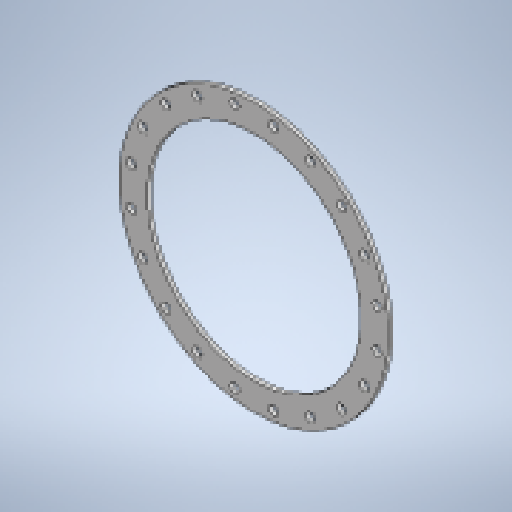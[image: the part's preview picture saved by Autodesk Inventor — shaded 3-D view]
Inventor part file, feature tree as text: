
AUTODESK INVENTOR PART (.ipt)
format: ipt  version: 2025.3 (Build 293356030, 356C)  size: 240,640 bytes
history: native  units: mm
features: sketch x2, other x2, extrude x1, pattern_circular x1, projected_geometry x1
ambient origin geometry x8: Origin, YZ Plane, XZ Plane, XY Plane, X Axis, Y Axis, Z Axis, Center Point
bodies: Solid1 (feature_tree)
feature tree (7):
  extrude  "Extrusion1"  Depth=10.0mm TaperAngle=0.0deg
  pattern_circular  "Circular Pattern1"  Count=31  [1 undecoded]
  sketch  "Sketch1"  dims[d0=512.0mm d1=670.0mm d2=10.0mm d3=0.0mm]
  sketch  "Sketch2"  dims[d4=533.0mm d5=310.0mm d7=23.0mm d8=10.0mm d9=10.0mm d10=0.0mm d11=200.0mm d12=360.0deg]
  projected_geometry  "Projected Loop1"
  other  "Cut1"
  other  "Definition1"
note: 1 required parameter value undecoded (feature->parameter linkage not recoverable at this tier; creation-order binding heuristic only, values carry confidence <= 0.55)
